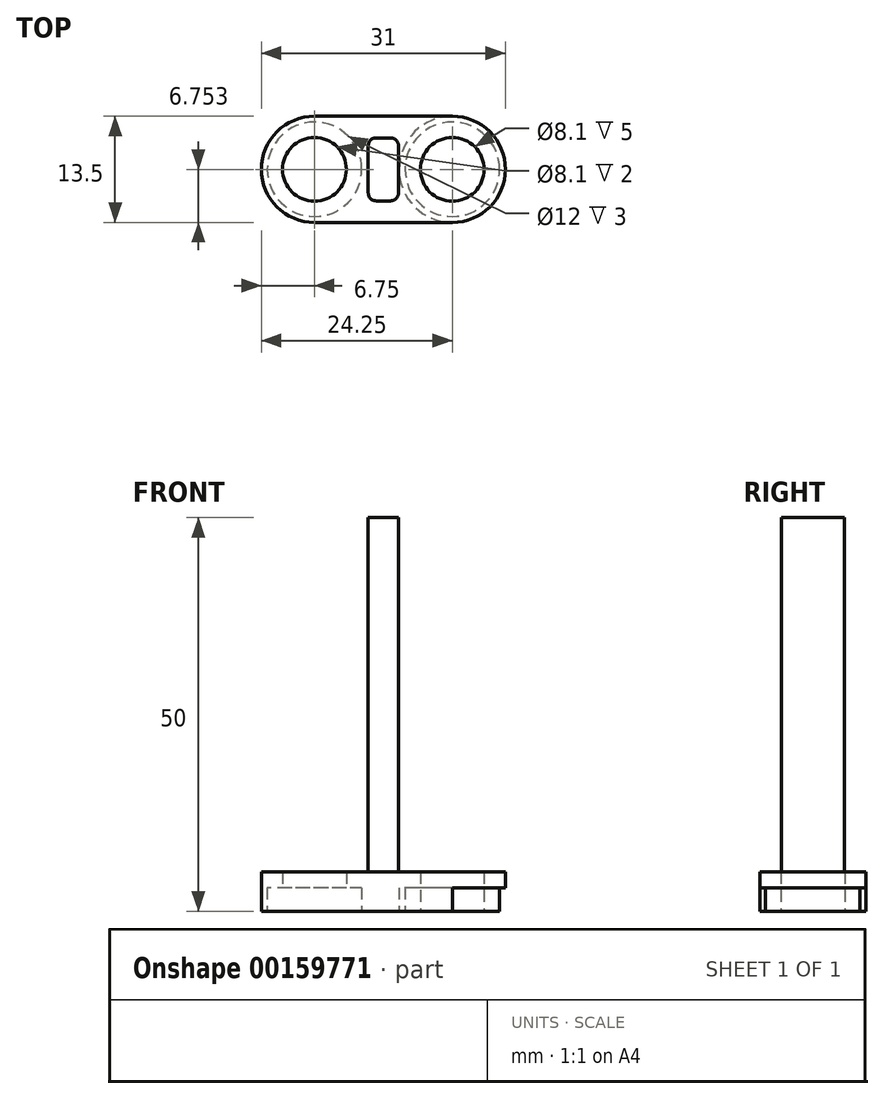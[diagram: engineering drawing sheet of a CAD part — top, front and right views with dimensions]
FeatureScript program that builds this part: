
annotation { "Feature Type Name" : "Feature", "Feature Type Description" : "" }
export const myFeature = defineFeature(function(context is Context, id is Id, definition is map)
    precondition{}
    {
        {
            var Q0;
            Q0=qCreatedBy(makeId("Top.planeOp"),FACE);
            var sketch = newSketch(context, id + "F0", { "sketchPlane" : qUnion([Q0])});
            skCircle(sketch, "E0", {"center": v(-8.75, 2.93) * mm, "radius": 4.05 * mm});
            skCircle(sketch, "E1", {"center": v(-8.75, 2.93) * mm, "radius": 6 * mm});
            skLineSegment(sketch, "E2", {"start": v(19.47, 2.93) * mm, "end": v(-27.45, 2.93) * mm, "construction": true});
            skCircle(sketch, "E3.MirrorC", {"center": v(8.75, 2.93) * mm, "radius": 6 * mm});
            skCircle(sketch, "E4.MirrorC", {"center": v(8.75, 2.93) * mm, "radius": 4.05 * mm});
            skCircle(sketch, "E5", {"center": v(-8.75, 2.93) * mm, "radius": 6.75 * mm});
            skCircle(sketch, "E6.MirrorC", {"center": v(8.75, 2.93) * mm, "radius": 6.75 * mm});
            skLineSegment(sketch, "E7", {"start": v(-8.75, 9.68) * mm, "end": v(8.75, 9.68) * mm});
            skLineSegment(sketch, "E8.MirrorCS", {"start": v(-8.75, -3.82) * mm, "end": v(8.75, -3.82) * mm});
            skLineSegment(sketch, "E9.bottom", {"start": v(1.92, 6.93) * mm, "end": v(-1.92, 6.93) * mm});
            skLineSegment(sketch, "E9.top", {"start": v(1.92, -1.07) * mm, "end": v(-1.92, -1.07) * mm});
            skLineSegment(sketch, "E9.left", {"start": v(1.92, 6.93) * mm, "end": v(1.92, -1.07) * mm});
            skLineSegment(sketch, "E9.right", {"start": v(-1.92, 6.93) * mm, "end": v(-1.92, -1.07) * mm});
            skPoint(sketch, "E9.middle", {"position": v(0, 2.93) * mm});
            skSolve(sketch);
        }
        {
            var Q0;
            {var subQ0=sQuery(id+"F0.wireOp",EDGE,"E7");Q0=makeQuery(id+"F0.imprint","IMPRINT",FACE,{"disambiguationData":[TD([[makeQuery(id+"F0.imprint","IMPRINT",EDGE,{"derivedFrom":subQ0}),-1.0]])]});}
            var Q1;
            Q1=makeQuery(id+"F0.imprint","IMPRINT",FACE,{"disambiguationData":[TD([[makeQuery(id+"F0.imprint","IMPRINT",EDGE,{"derivedFrom":sQuery(id+"F0.wireOp",EDGE,"E1")}),-1.0]])]});
            var Q2;
            Q2=makeQuery(id+"F0.imprint","IMPRINT",FACE,{"disambiguationData":[TD([[makeQuery(id+"F0.imprint","IMPRINT",EDGE,{"derivedFrom":sQuery(id+"F0.wireOp",EDGE,"E3.MirrorC")}),1.0]])]});
            var Q3;
            Q3=makeQuery(id+"F0.imprint","IMPRINT",FACE,{"disambiguationData":[TD([[makeQuery(id+"F0.imprint","IMPRINT",EDGE,{"derivedFrom":sQuery(id+"F0.wireOp",EDGE,"E0")}),-1.0]])]});
            var Q4;
            Q4=makeQuery(id+"F0.imprint","IMPRINT",FACE,{"disambiguationData":[TD([[makeQuery(id+"F0.imprint","IMPRINT",EDGE,{"derivedFrom":sQuery(id+"F0.wireOp",EDGE,"E3.MirrorC")}),-1.0]])]});
            extrude(context, id + "F1", {"entities" : qUnion([Q0, Q1, Q2, Q3, Q4]), "depth" : 5 * mm});
        }
        {
            var Q0;
            Q0=makeQuery(id+"F0.imprint","IMPRINT",FACE,{"disambiguationData":[TD([[makeQuery(id+"F0.imprint","IMPRINT",EDGE,{"derivedFrom":sQuery(id+"F0.wireOp",EDGE,"E0")}),-1.0]])]});
            var Q1;
            Q1=makeQuery(id+"F0.imprint","IMPRINT",FACE,{"disambiguationData":[TD([[makeQuery(id+"F0.imprint","IMPRINT",EDGE,{"derivedFrom":sQuery(id+"F0.wireOp",EDGE,"E3.MirrorC")}),-1.0]])]});
            extrude(context, id + "F2", {"entities" : qUnion([Q0, Q1]), "operationType" : NewBodyOperationType.REMOVE, "depth" : 3 * mm});
        }
        {
            var Q0;
            Q0=makeQuery(id+"F0.imprint","IMPRINT",FACE,{"disambiguationData":[TD([[makeQuery(id+"F0.imprint","IMPRINT",EDGE,{"derivedFrom":sQuery(id+"F0.wireOp",EDGE,"E9.bottom")}),1.0]])]});
            extrude(context, id + "F3", {"entities" : qUnion([Q0]), "operationType" : NewBodyOperationType.ADD, "depth" : 50 * mm});
        }
        {
            var Q0;
            Q0=makeQuery(id+"F3.opExtrude","SWEPT_EDGE",EDGE,{"disambiguationData":[OSD([sQuery(id+"F0.wireOp",EDGE,"E9.top"),sQuery(id+"F0.wireOp",EDGE,"E9.right")])]});
            var Q1;
            Q1=makeQuery(id+"F3.opExtrude","SWEPT_EDGE",EDGE,{"disambiguationData":[OSD([sQuery(id+"F0.wireOp",EDGE,"E9.top"),sQuery(id+"F0.wireOp",EDGE,"E9.left")])]});
            var Q2;
            Q2=makeQuery(id+"F3.opExtrude","SWEPT_EDGE",EDGE,{"disambiguationData":[OSD([sQuery(id+"F0.wireOp",EDGE,"E9.bottom"),sQuery(id+"F0.wireOp",EDGE,"E9.left")])]});
            var Q3;
            Q3=makeQuery(id+"F3.opExtrude","SWEPT_EDGE",EDGE,{"disambiguationData":[OSD([sQuery(id+"F0.wireOp",EDGE,"E9.bottom"),sQuery(id+"F0.wireOp",EDGE,"E9.right")])]});
            fillet(context, id + "F4", {"entities" : qUnion([Q0, Q1, Q2, Q3]), "radius" : 1 * mm, "tangentPropagation" : true, "allowEdgeOverflow" : false});
        }
    });
